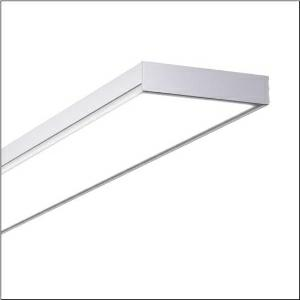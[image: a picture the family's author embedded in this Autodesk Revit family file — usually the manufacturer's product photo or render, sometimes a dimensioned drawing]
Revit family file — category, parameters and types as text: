
# Revit family: apollon_31_surface_51mp25wd2441e
name_source: partatom
category: Lighting Fixtures
units: mm (PartAtom-declared; Revit-internal decimal feet)

## family parameters
Cut with Voids When Loaded = No
Host = Face
Light Source = No
Part Type = Normal
Room Calculation Point = No
Round Connector Dimension = Use Diameter
Shared = No

## types (1)
- Apollon 31 Surface (1 x LED, 3800 lm, 28 W, 4000K)
    Apparent Load = 28 VA
    CIE Flux Codes = 61 87 97 97 100
    Color Rendering = 80
    Color Temperature = 4000K
    Default Elevation = 1800 mm
    Description = Apollon 31 Surface, office luminaire, primary optical cover: micro prismatic cover, of PMMA, light emission: direct distribution, primary light characteristic: symmetric, installation type: surface-mounted, LED, rated luminous flux: 3.800lm, luminous efficacy: 134lm/W, light colour: 840, colour temperature: 4000K, control gear: DALI 2, with terminal, 5-pole, mains connection: 220..240V, AC, 50/60Hz, rated input power: 28W, housing, of sheet steel, coated, metallic grey (RAL 9006), length: 1.245mm, width: 200mm, height: 44mm, protection rating (complete): IP20, protection rating (on room side): IP40, protection rating (lamp compartment, on room side): IP40, insulation class (complete): insulation class I (protective earthing), certification: CE, ENEC, UKCA, impact resistance: IK02, permissible operating ambient temperature: -20..+40°C, standard: EN 60598-2-22, packaging unit: 1 piece
    Height = 44 mm
    Lamp = 1 x LED
    Lamp Light Flux = 3800 lm
    Lamp Power = 28 W
    Lamp count = 1
    Length = 1245 mm
    Luminous efficacy = 136 lm/W
    Manufacturer = Siteco
    ModVariant = No
    Model = 51MP25WD2441E
    Mounting Place = Ceiling
    Mounting Type = Surface mounted
    Number of Poles = 1
    OnlyDefault = Yes
    Power Factor = 1
    Product Name = Apollon 31 Surface
    Product group = office luminaire | ceiling mounted
    ProductGroupID = 301
    Protection Class = Protection class I
    Protection Degree = IP 20
    RLX_Detail_Level = 1
    RLX_Emergency_Light_Flux = 0 lm
    RLX_Emergency_Type = 0
    RLX_Emergency_Type_DB = No
    RlxData = <blob elided: 24133 chars, md5=75bb36eb>
    Socket = socket
    Standby Power = 0 W
    System Light Flux = 3800 lm
    System Power = 28 W
    Type Comments = Product without accessories
    Type Image = l_1313654.jpg
    URL = http://relux.com
    VarID = ---
    Voltage = 0 V
    Weight = 0.00 kg
    Width = 200 mm  [stored 0.656168 ft]

note: [stored X ft] marks values corroborated as IEEE doubles in the binary element streams (Revit-internal decimal feet)

## geometry (parser evidence)
native form markers: Blend x4, Sweep x9
no freeform markers — native parametric forms only
